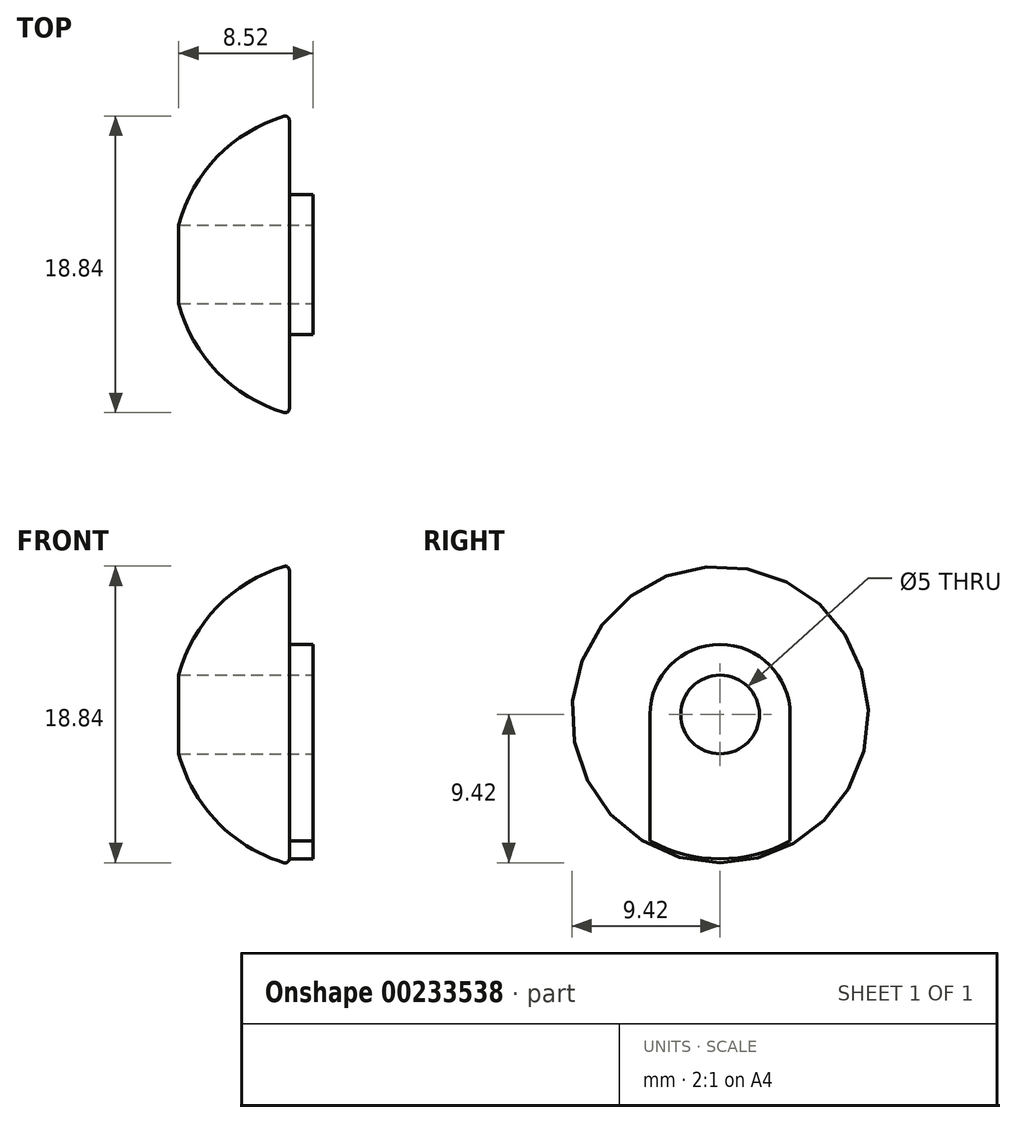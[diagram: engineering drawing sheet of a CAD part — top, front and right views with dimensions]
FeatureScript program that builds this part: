
annotation { "Feature Type Name" : "Feature", "Feature Type Description" : "" }
export const myFeature = defineFeature(function(context is Context, id is Id, definition is map)
    precondition{}
    {
        {
            var Q0;
            Q0=qCreatedBy(makeId("Front.planeOp"),FACE);
            var sketch = newSketch(context, id + "F0", { "sketchPlane" : qUnion([Q0])});
            skLineSegment(sketch, "E0", {"start": v(0, 4.45) * mm, "end": v(0, 9.5) * mm, "construction": true});
            skLineSegment(sketch, "E1", {"start": v(0, 0) * mm, "end": v(0, 9.5) * mm});
            skLineSegment(sketch, "E2", {"start": v(-7.34, 0) * mm, "end": v(-7.34, -20.68) * mm, "construction": true});
            skLineSegment(sketch, "E3", {"start": v(0, 9.5) * mm, "end": v(18.63, 14.35) * mm, "construction": true});
            skArc(sketch, "E4", {"start": v(0, 9.5) * mm, "mid": v(-5.3, 6) * mm, "end": v(-7.34, 0) * mm});
            skLineSegment(sketch, "E5", {"start": v(0, 4.45) * mm, "end": v(4, 4.45) * mm});
            skLineSegment(sketch, "E6", {"start": v(4, 4.45) * mm, "end": v(4, 0) * mm});
            skLineSegment(sketch, "E7", {"start": v(4, 0) * mm, "end": v(-7.34, 0) * mm});
            skLineSegment(sketch, "E8", {"start": v(-6.3, 0) * mm, "end": v(-6.3, 4.4) * mm, "construction": true});
            skSolve(sketch);
        }
        {
            var Q0;
            Q0 = qSketchRegion(id + "F0", true);
            var Q1;
            Q1=sQuery(id+"F0.wireOp",EDGE,"E7");
            revolve(context, id + "F1", {"entities" : qUnion([Q0]), "axis" : qUnion([Q1]), "revolveType" : RevolveType.FULL});
        }
        {
            var Q0;
            Q0=makeQuery(id+"F4.boolean.opBoolean","SPLIT",EDGE,{"derivedFrom":makeQuery(id+"F1.opRevolve","SWEPT_EDGE",EDGE,{"disambiguationData":[OSD([sQuery(id+"F0.wireOp",EDGE,"E1"),sQuery(id+"F0.wireOp",EDGE,"E4")])]})});
            fillet(context, id + "F2", {"entities" : qUnion([Q0]), "radius" : 0.25 * mm, "tangentPropagation" : true, "allowEdgeOverflow" : false});
        }
        {
            var Q0;
            Q0=qCreatedBy(makeId("Right.planeOp"),FACE);
            var sketch = newSketch(context, id + "F3", { "sketchPlane" : qUnion([Q0])});
            skArc(sketch, "E9.0", {"start": v(-4.45, 0) * mm, "mid": v(0, -4.45) * mm, "end": v(4.45, 0) * mm});
            skArc(sketch, "E10.0", {"start": v(-4.45, -8.02) * mm, "mid": v(0, -9.17) * mm, "end": v(4.45, -8.02) * mm});
            skLineSegment(sketch, "E11", {"start": v(-4.45, 0) * mm, "end": v(-4.45, -8.02) * mm});
            skLineSegment(sketch, "E12", {"start": v(4.45, 0) * mm, "end": v(4.45, -8.02) * mm});
            skSolve(sketch);
        }
        {
            var Q0;
            Q0 = qSketchRegion(id + "F3", true);
            var Q1;
            Q1=makeQuery(id+"F1.opRevolve","SWEPT_FACE",FACE,{"disambiguationData":[OSD([sQuery(id+"F0.wireOp",EDGE,"E6")])]});
            extrude(context, id + "F4", {"entities" : qUnion([Q0]), "operationType" : NewBodyOperationType.ADD, "endBound" : BoundingType.UP_TO_SURFACE, "endBoundEntityFace" : qUnion([Q1]), "depth" : 25 * mm});
        }
        {
            var Q0;
            Q0=qCreatedBy(makeId("Right.planeOp"),FACE);
            var sketch = newSketch(context, id + "F5", { "sketchPlane" : qUnion([Q0])});
            skCircle(sketch, "E13", {"center": v(0, 0) * mm, "radius": 2.5 * mm});
            skSolve(sketch);
        }
        {
            var Q0;
            Q0 = qSketchRegion(id + "F5", true);
            extrude(context, id + "F6", {"entities" : qUnion([Q0]), "operationType" : NewBodyOperationType.REMOVE, "endBound" : BoundingType.THROUGH_ALL, "oppositeDirection" : true, "depth" : 25 * mm, "hasSecondDirection" : true, "secondDirectionOppositeDirection" : false, "secondDirectionDepth" : 25 * mm});
        }
        {
            var Q0;
            Q0=makeQuery(id+"F4.boolean.opBoolean","MERGE",FACE,{"derivedFrom":[makeQuery(id+"F1.opRevolve","SWEPT_FACE",FACE,{"disambiguationData":[OSD([sQuery(id+"F0.wireOp",EDGE,"E6")])]}),makeQuery(id+"F4.opExtrude","CAP_FACE",FACE,{"disambiguationData":[OSD([sQuery(id+"F3.wireOp",EDGE,"E9.0"),sQuery(id+"F3.wireOp",EDGE,"E10.0"),sQuery(id+"F3.wireOp",EDGE,"E11"),sQuery(id+"F3.wireOp",EDGE,"E12")])],"isStart":false})]});
            cPlane(context, id + "F7", {"entities" : qUnion([Q0]), "cplaneType" : CPlaneType.OFFSET, "offset" : 2.5 * mm, "oppositeDirection" : true, "width" : 150 * mm, "height" : 150 * mm});
        }
        {
            var Q0;
            Q0=qCreatedBy(id+"F7.planeOp",FACE);
            var sketch = newSketch(context, id + "F8", { "sketchPlane" : qUnion([Q0])});
            skArc(sketch, "E14.0", {"start": v(4.45, 0) * mm, "mid": v(0, 4.45) * mm, "end": v(-4.45, 0) * mm});
            skCircle(sketch, "E15", {"center": v(0, 0) * mm, "radius": 4.45 * mm, "construction": true});
            skLineSegment(sketch, "E16", {"start": v(-4.44, -4.45) * mm, "end": v(4.48, -4.45) * mm, "construction": true});
            skLineSegment(sketch, "E17", {"start": v(-4.45, -14.45) * mm, "end": v(4.45, -14.45) * mm});
            skLineSegment(sketch, "E18", {"start": v(-4.45, -14.45) * mm, "end": v(-4.45, 0) * mm});
            skLineSegment(sketch, "E19", {"start": v(4.45, 0) * mm, "end": v(4.45, -14.45) * mm});
            skSolve(sketch);
        }
        {
            var Q0;
            Q0 = qSketchRegion(id + "F8", true);
            extrude(context, id + "F9", {"entities" : qUnion([Q0]), "operationType" : NewBodyOperationType.REMOVE, "depth" : 3 * mm, "offsetDistance" : 25 * mm});
        }
    });
